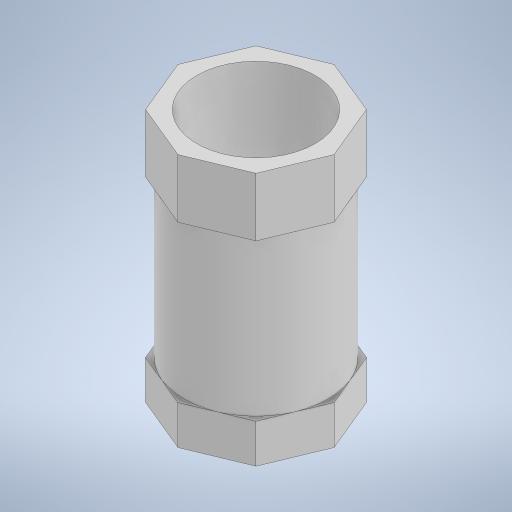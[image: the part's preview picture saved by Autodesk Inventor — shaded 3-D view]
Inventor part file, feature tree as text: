
AUTODESK INVENTOR PART (.ipt)
format: ipt  version: 2024 (Build 280153000, 153)  size: 293,888 bytes
history: native  units: mm
features: other x3, extrude x3, hole x1, sketch x1
ambient origin geometry x8: Origin, YZ Plane, XZ Plane, XY Plane, X Axis, Y Axis, Z Axis, Center Point
bodies: Body1 (feature_tree)
feature tree (8):
  other  "Sólido1"
  extrude  "Extrusión1"  Depth=10.0mm TaperAngle=0.0deg
  extrude  "Extrusión2"  Depth=10.0mm TaperAngle=0.0deg
  extrude  "Extrusión3"  Depth=10.0mm
  hole  "Agujero1"  [1 undecoded]
  other  "Edición directa1"
  sketch  "Boceto1"  dims[d0=20.0mm d1=5.0mm d2=0.0mm d3=20.0mm d4=0.0mm d5=20.0mm d6=7.5mm d7=0.0mm d8=15.1638mm d9=32.5mm d10=4.0mm d11=2.0mm d12=90.0deg d13=8.0mm d14=20.594885mm d15=2.666666mm d16=10.0mm d17=10.0mm]
  other  "Escala1"
note: 1 required parameter value undecoded (feature->parameter linkage not recoverable at this tier; creation-order binding heuristic only, values carry confidence <= 0.55)
